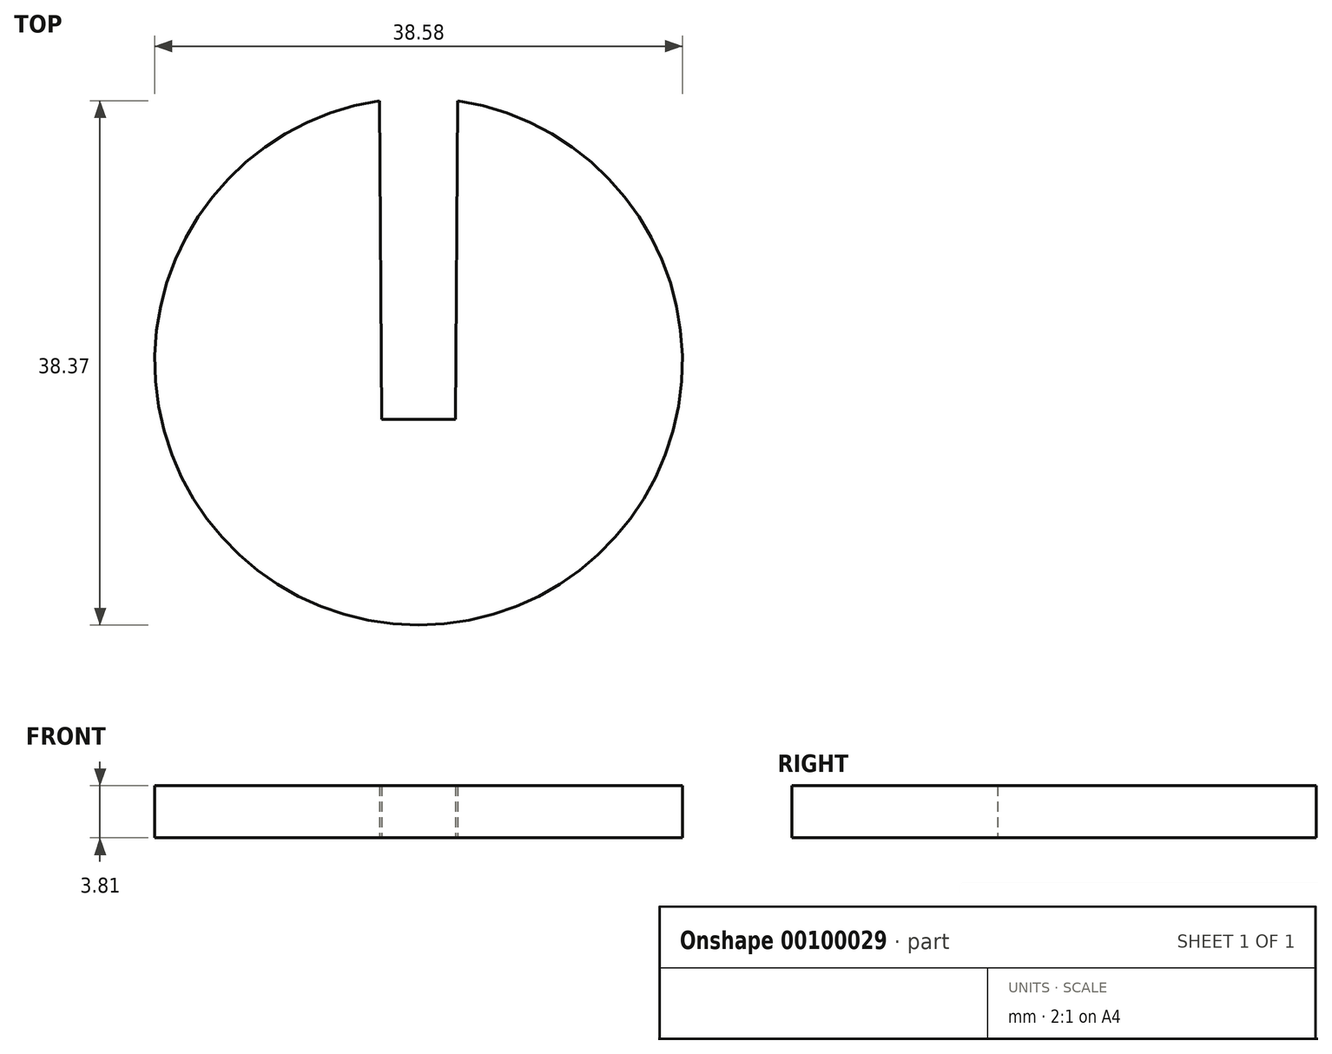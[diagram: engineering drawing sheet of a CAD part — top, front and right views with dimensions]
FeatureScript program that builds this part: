
annotation { "Feature Type Name" : "Feature", "Feature Type Description" : "" }
export const myFeature = defineFeature(function(context is Context, id is Id, definition is map)
    precondition{}
    {
        {
            var Q0;
            Q0=qCreatedBy(makeId("Top.planeOp"),FACE);
            var sketch = newSketch(context, id + "F0", { "sketchPlane" : qUnion([Q0])});
            skLineSegment(sketch, "E0.bottom", {"start": v(-2.68, 50.05) * mm, "end": v(2.68, 50.05) * mm});
            skLineSegment(sketch, "E0.top", {"start": v(-2.68, -18.18) * mm, "end": v(2.68, -18.18) * mm});
            skLineSegment(sketch, "E0.left", {"start": v(-2.68, 50.05) * mm, "end": v(-2.68, -18.18) * mm});
            skLineSegment(sketch, "E0.right", {"start": v(2.68, 50.05) * mm, "end": v(2.68, -18.18) * mm});
            skSolve(sketch);
        }
        {
            var Q0;
            Q0=qCreatedBy(makeId("Top.planeOp"),FACE);
            var sketch = newSketch(context, id + "F1", { "sketchPlane" : qUnion([Q0])});
            skArc(sketch, "E1", {"start": v(-2.87, 5.3) * mm, "mid": v(0, -33.08) * mm, "end": v(2.87, 5.3) * mm});
            skPoint(sketch, "E2", {"position": v(-2.87, 5.3) * mm});
            skPoint(sketch, "E3", {"position": v(2.87, 5.3) * mm});
            skPoint(sketch, "E4", {"position": v(-2.68, -18.01) * mm});
            skPoint(sketch, "E5", {"position": v(2.68, -18.01) * mm});
            skLineSegment(sketch, "E6", {"start": v(-2.87, 5.3) * mm, "end": v(-2.68, -18.01) * mm});
            skLineSegment(sketch, "E7", {"start": v(-2.68, -18.01) * mm, "end": v(2.68, -18.01) * mm});
            skLineSegment(sketch, "E8", {"start": v(2.68, -18.01) * mm, "end": v(2.87, 5.3) * mm});
            skSolve(sketch);
        }
        {
            var Q0;
            Q0=sQuery(id+"F0.wireOp",EDGE,"E0.top");
            extrude(context, id + "F2", {"bodyType" : ToolBodyType.SURFACE, "surfaceEntities" : qUnion([Q0]), "depth" : 3.8 * mm});
        }
        {
            var Q0;
            Q0 = qSketchRegion(id + "F1", true);
            extrude(context, id + "F3", {"entities" : qUnion([Q0]), "depth" : 3.8 * mm});
        }
    });
